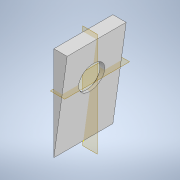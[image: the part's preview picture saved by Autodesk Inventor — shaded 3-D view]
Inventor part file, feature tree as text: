
AUTODESK INVENTOR PART (.ipt)
format: ipt  version: 2021 (Build 250183000, 183)  size: 408,576 bytes
history: native  units: in
note: dims shown in document units (in); Inventor stores cm internally (conversion verified against a paired STEP export)
features: sketch x7, extrude x6, plane x2
ambient origin geometry x8: Origin, YZ Plane, XZ Plane, XY Plane, X Axis, Y Axis, Z Axis, Center Point
bodies: Solid1 (feature_tree)
feature tree (15):
  extrude  "MainStructure"  Depth=0.5622in
  extrude  "PipeHole"  TaperAngle=0.0deg  [1 undecoded]
  extrude  "TextForSmallText"  TaperAngle=0.0deg  [1 undecoded]
  extrude  "TextForBack"  Depth=0.375in
  extrude  "ReliefForHole"  TaperAngle=45.0deg  [1 undecoded]
  plane  "Work Plane1"
  plane  "Work Plane2"
  sketch  "Sketch11"  dims[d42=2.5in]
  extrude  "SideAngle"  TaperAngle=0.0deg  [1 undecoded]
  sketch  "Sketch1"  dims[d1=0.055in d2=0.5622in]
  sketch  "Sketch2"  dims[d4=0.0in d7=0.0in d8=0.0in]
  sketch  "Sketch7"  dims[d25=0.0in d28=0.0in]
  sketch  "Sketch8"  dims[d29=0.0in d35=0.375in]
  sketch  "Sketch9"  dims[d36=0.1in d37=0.0in d38=45.0deg]
  sketch  "Sketch10"  dims[d39=45.0deg d40=0.0in d41=0.0in]
note: 4 required parameter values undecoded (feature->parameter linkage not recoverable at this tier; creation-order binding heuristic only, values carry confidence <= 0.55)
